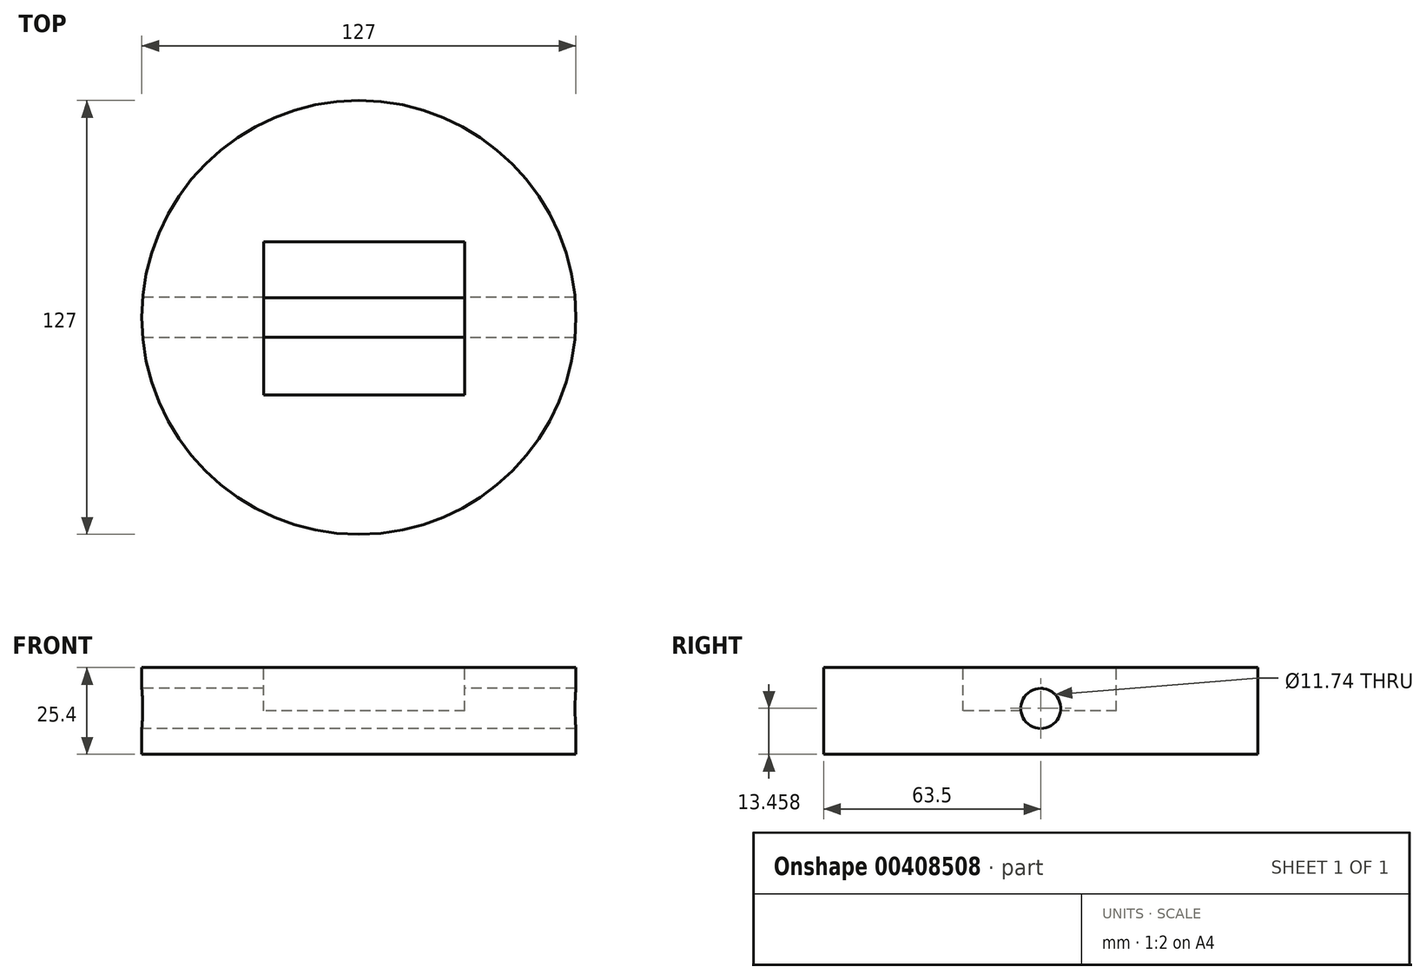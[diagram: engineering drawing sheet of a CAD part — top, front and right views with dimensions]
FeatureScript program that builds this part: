
annotation { "Feature Type Name" : "Feature", "Feature Type Description" : "" }
export const myFeature = defineFeature(function(context is Context, id is Id, definition is map)
    precondition{}
    {
        {
            var Q0;
            Q0=qCreatedBy(makeId("Top.planeOp"),FACE);
            var sketch = newSketch(context, id + "F0", { "sketchPlane" : qUnion([Q0])});
            skCircle(sketch, "E0", {"center": v(0, 0) * mm, "radius": 63.5 * mm});
            skSolve(sketch);
        }
        {
            var Q0;
            Q0=makeQuery(id+"F0.imprint","IMPRINT",FACE,{"disambiguationData":[TD([[makeQuery(id+"F0.imprint","IMPRINT",EDGE,{"derivedFrom":sQuery(id+"F0.wireOp",EDGE,"E0")}),1.0]])]});
            extrude(context, id + "F1", {"entities" : qUnion([Q0]), "depth" : 25.4 * mm});
        }
        {
            var Q0;
            Q0=makeQuery(id+"F1.opExtrude","CAP_FACE",FACE,{"disambiguationData":[OSD([sQuery(id+"F0.wireOp",EDGE,"E0")])],"isStart":false});
            var sketch = newSketch(context, id + "F2", { "sketchPlane" : qUnion([Q0])});
            skLineSegment(sketch, "E1.bottom", {"start": v(-27.84, 22.12) * mm, "end": v(30.97, 22.12) * mm});
            skLineSegment(sketch, "E1.top", {"start": v(-27.84, -22.68) * mm, "end": v(30.97, -22.68) * mm});
            skLineSegment(sketch, "E1.left", {"start": v(-27.84, 22.12) * mm, "end": v(-27.84, -22.68) * mm});
            skLineSegment(sketch, "E1.right", {"start": v(30.97, 22.12) * mm, "end": v(30.97, -22.68) * mm});
            skSolve(sketch);
        }
        {
            var Q0;
            Q0=makeQuery(id+"F2.imprint","IMPRINT",FACE,{"disambiguationData":[TD([[makeQuery(id+"F2.imprint","IMPRINT",EDGE,{"derivedFrom":sQuery(id+"F2.wireOp",EDGE,"E1.bottom")}),-1.0]])]});
            extrude(context, id + "F3", {"entities" : qUnion([Q0]), "operationType" : NewBodyOperationType.REMOVE, "oppositeDirection" : true, "depth" : 12.7 * mm});
        }
        {
            var Q0;
            Q0=qCreatedBy(makeId("Right.planeOp"),FACE);
            var sketch = newSketch(context, id + "F4", { "sketchPlane" : qUnion([Q0])});
            skCircle(sketch, "E2", {"center": v(0, 13.46) * mm, "radius": 5.87 * mm});
            skSolve(sketch);
        }
        {
            var Q0;
            Q0=makeQuery(id+"F4.imprint","IMPRINT",FACE,{"disambiguationData":[TD([[makeQuery(id+"F4.imprint","IMPRINT",EDGE,{"derivedFrom":sQuery(id+"F4.wireOp",EDGE,"E2")}),1.0]])]});
            extrude(context, id + "F5", {"entities" : qUnion([Q0]), "operationType" : NewBodyOperationType.REMOVE, "endBound" : BoundingType.SYMMETRIC, "depth" : 254 * mm});
        }
    });
